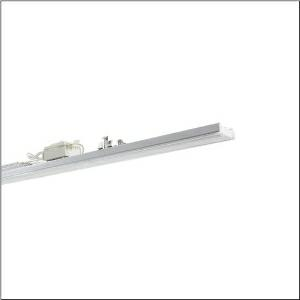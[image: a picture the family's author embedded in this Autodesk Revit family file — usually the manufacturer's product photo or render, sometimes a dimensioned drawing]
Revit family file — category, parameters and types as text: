
# Revit family: licross_r__11_recessed_mo_51te12dv475g_2d86
name_source: partatom
category: Lighting Fixtures
units: mm (PartAtom-declared; Revit-internal decimal feet)

## family parameters
Cut with Voids When Loaded = No
Host = Face
Light Source = No
Part Type = Normal
Room Calculation Point = No
Round Connector Dimension = Use Diameter
Shared = No

## types (1)
- --- (1 x LED, 7640 lm, 40.1 W, 4000K)
    Apparent Load = 40 VA
    CIE Flux Codes = 67 92 99 100 100
    Color Rendering = 80
    Color Temperature = 4000K
    Default Elevation = 1800 mm
    Description = Licross® 11 Recessed MO, luminaire insert, of sheet steel, galvanised, coil coated, white, length: 2.250mm, width: 66mm, height: 67mm, LED rated luminous flux: 7.640lm, light colour: 840, control gear: DALI 2, with plug, 5-pole, with phase selection, mains connection: 220..240V, AC, 50/60Hz, rated input power: 40W, halogen-free wiring, primary optical cover: cover, of PMMA, light emission: direct distribution, primary light characteristic: symmetric, protection rating (complete): IP54, insulation class (complete): insulation class I (protective earthing), certification: CE, ENEC, VDE, UKCA, protection symbol: D if used in an environment with non-conductive dust loads with corresponding accessories, impact resistance: IK06, permissible ambient temperature for indoor applications: -25..+45°C, corresponds to IFS (International Featured Standards) requirements for safety and quality in the food industry, reducing of maximum allowable ambient temperature of 5°C with ceiling mounting, LABS conformity tested according to VDMA 24364:2018-05, packaging unit: 1 piece
    Height = 58 mm
    Lamp = 1 x LED
    Lamp Light Flux = 7640 lm
    Lamp Power = 40.1 W
    Lamp count = 1
    Length = 2250 mm
    Luminous efficacy = 191 lm/W
    Manufacturer = Siteco
    ModVariant = No
    Model = 51TE12DV475G
    Mounting Place = Ceiling
    Mounting Type = Pendant
    Number of Poles = 1
    OnlyDefault = Yes
    Power Factor = 1
    Product Name = Licross® 11 Recessed MO
    Product group = luminaire insert
    ProductGroupID = 902
    Protection Class = Protection class I
    Protection Degree = IP 54
    RLX_Detail_Level = 1
    RLX_Emergency_Light_Flux = 0 lm
    RLX_Emergency_Type = 0
    RLX_Emergency_Type_DB = No
    RlxData = <blob elided: 29001 chars, md5=4d6ad72a>
    Socket = socket
    Standby Power = 0 W
    System Light Flux = 7640 lm
    System Power = 40 W
    Type Comments = factory setting: luminous flux: 100 % | dim-lin: 254 | 180 mA
    Type Image = l_1296930.jpg
    URL = http://relux.com
    VarID = @adj_100232
    Voltage = 0 V
    Weight = 0.00 kg
    Width = 66 mm

## geometry (parser evidence)
native form markers: Blend x4, Sweep x10
no freeform markers — native parametric forms only
